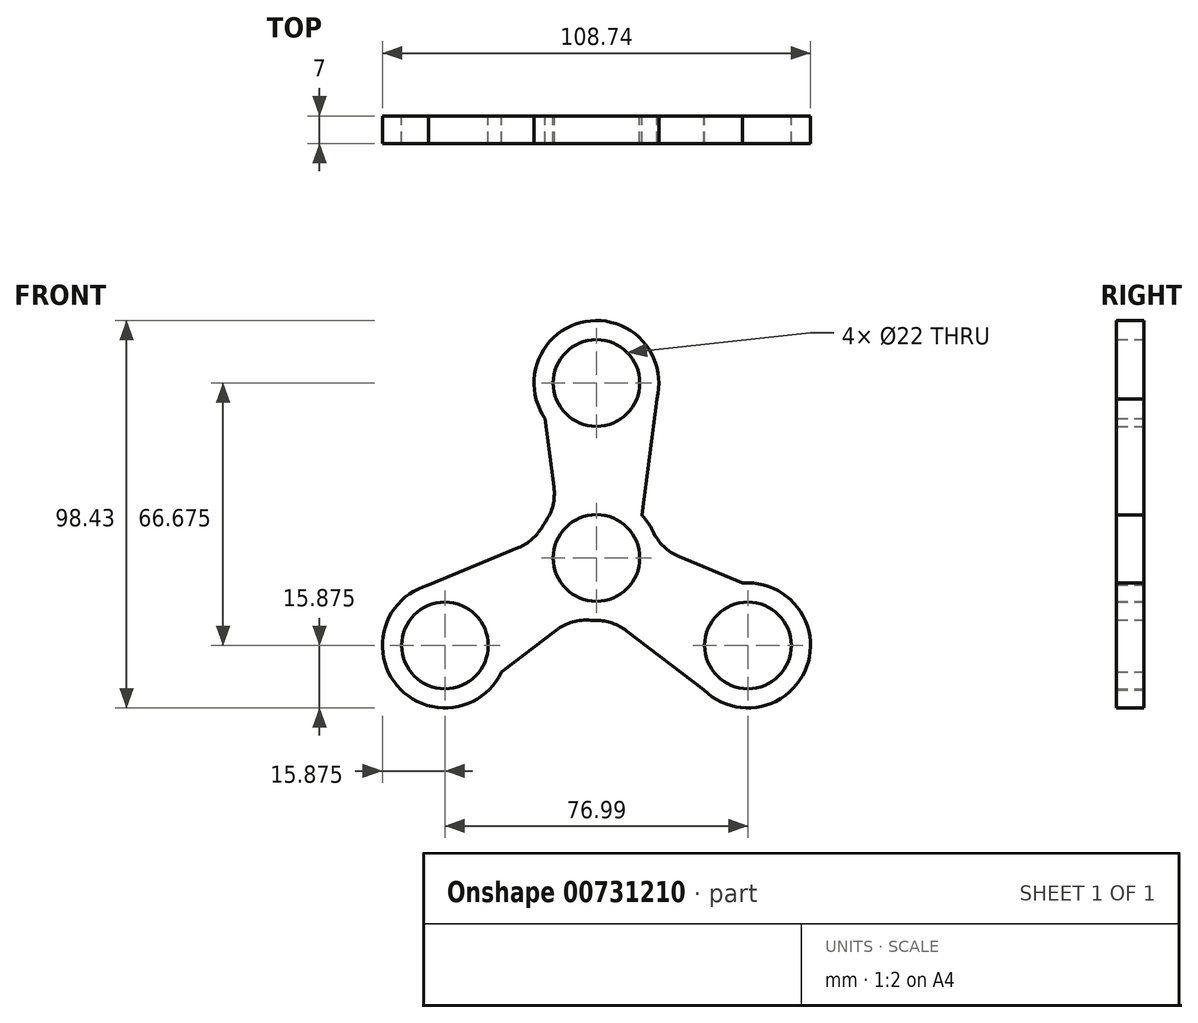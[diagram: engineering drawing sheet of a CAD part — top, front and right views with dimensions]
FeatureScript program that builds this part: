
annotation { "Feature Type Name" : "Feature", "Feature Type Description" : "" }
export const myFeature = defineFeature(function(context is Context, id is Id, definition is map)
    precondition{}
    {
        {
            var Q0;
            Q0=qCreatedBy(makeId("Front.planeOp"),FACE);
            var sketch = newSketch(context, id + "F0", { "sketchPlane" : qUnion([Q0])});
            skCircle(sketch, "E0", {"center": v(0, 0) * mm, "radius": 11 * mm});
            skArc(sketch, "E1", {"start": v(-1.4, -15.81) * mm, "mid": v(-0.72, -15.86) * mm, "end": v(-0.04, -15.87) * mm});
            skCircle(sketch, "E2", {"center": v(0, 44.45) * mm, "radius": 11 * mm});
            skCircle(sketch, "E3", {"center": v(0, 44.45) * mm, "radius": 15.88 * mm});
            skLineSegment(sketch, "E4", {"start": v(15.88, 44.45) * mm, "end": v(11.55, 10.9) * mm});
            skLineSegment(sketch, "E5.MirrorCS", {"start": v(-14.3, 45.18) * mm, "end": v(-10.8, 18.03) * mm});
            skLineSegment(sketch, "E6.1.0", {"start": v(-46.43, -8.48) * mm, "end": v(-19.82, 2.63) * mm});
            skCircle(sketch, "E6.1.1", {"center": v(-38.5, -22.23) * mm, "radius": 15.88 * mm});
            skCircle(sketch, "E6.1.2", {"center": v(-38.5, -22.23) * mm, "radius": 11 * mm});
            skLineSegment(sketch, "E6.1.3", {"start": v(-31.98, -34.97) * mm, "end": v(-10.22, -18.37) * mm});
            skLineSegment(sketch, "E6.2.0", {"start": v(30.56, -35.97) * mm, "end": v(7.63, -18.48) * mm});
            skCircle(sketch, "E6.2.1", {"center": v(38.5, -22.22) * mm, "radius": 15.87 * mm});
            skCircle(sketch, "E6.2.2", {"center": v(38.5, -22.22) * mm, "radius": 11 * mm});
            skLineSegment(sketch, "E6.2.3", {"start": v(46.27, -10.2) * mm, "end": v(21.02, 0.33) * mm});
            skLineSegment(sketch, "E6.anchor1", {"start": v(0, 0) * mm, "end": v(11.55, 10.9) * mm, "construction": true});
            skLineSegment(sketch, "E6.anchor2", {"start": v(0, 0) * mm, "end": v(3.66, -15.45) * mm, "construction": true});
            skArc(sketch, "E7.trimOffspring", {"start": v(-13, 9.12) * mm, "mid": v(-13.37, 8.55) * mm, "end": v(-13.73, 7.97) * mm});
            skArc(sketch, "E8.trimOffspring", {"start": v(14.4, 6.7) * mm, "mid": v(13.14, 8.9) * mm, "end": v(11.55, 10.9) * mm});
            skPoint(sketch, "E9.visualSharp", {"position": v(-5.6, -14.85) * mm});
            skArc(sketch, "E9.filletArc", {"start": v(-1.4, -15.81) * mm, "mid": v(-6.05, -16.27) * mm, "end": v(-10.22, -18.37) * mm});
            skPoint(sketch, "E10.visualSharp", {"position": v(3.66, -15.45) * mm});
            skArc(sketch, "E10.filletArc", {"start": v(7.63, -18.48) * mm, "mid": v(4, -16.55) * mm, "end": v(-0.04, -15.87) * mm});
            skPoint(sketch, "E11.visualSharp", {"position": v(-15.2, 4.56) * mm});
            skArc(sketch, "E11.filletArc", {"start": v(-19.82, 2.63) * mm, "mid": v(-16.33, 4.8) * mm, "end": v(-13.73, 7.97) * mm});
            skPoint(sketch, "E12.visualSharp", {"position": v(-10.06, 12.28) * mm});
            skArc(sketch, "E12.filletArc", {"start": v(-13, 9.12) * mm, "mid": v(-11.06, 13.37) * mm, "end": v(-10.8, 18.03) * mm});
            skPoint(sketch, "E13.visualSharp", {"position": v(15.67, 2.57) * mm});
            skArc(sketch, "E13.filletArc", {"start": v(14.4, 6.7) * mm, "mid": v(17.1, 2.9) * mm, "end": v(21.02, 0.33) * mm});
            skSolve(sketch);
        }
        {
            var Q0;
            Q0 = qSketchRegion(id + "F0", true);
            extrude(context, id + "F1", {"entities" : qUnion([Q0]), "depth" : 7 * mm, "offsetDistance" : 25.4 * mm});
        }
    });
